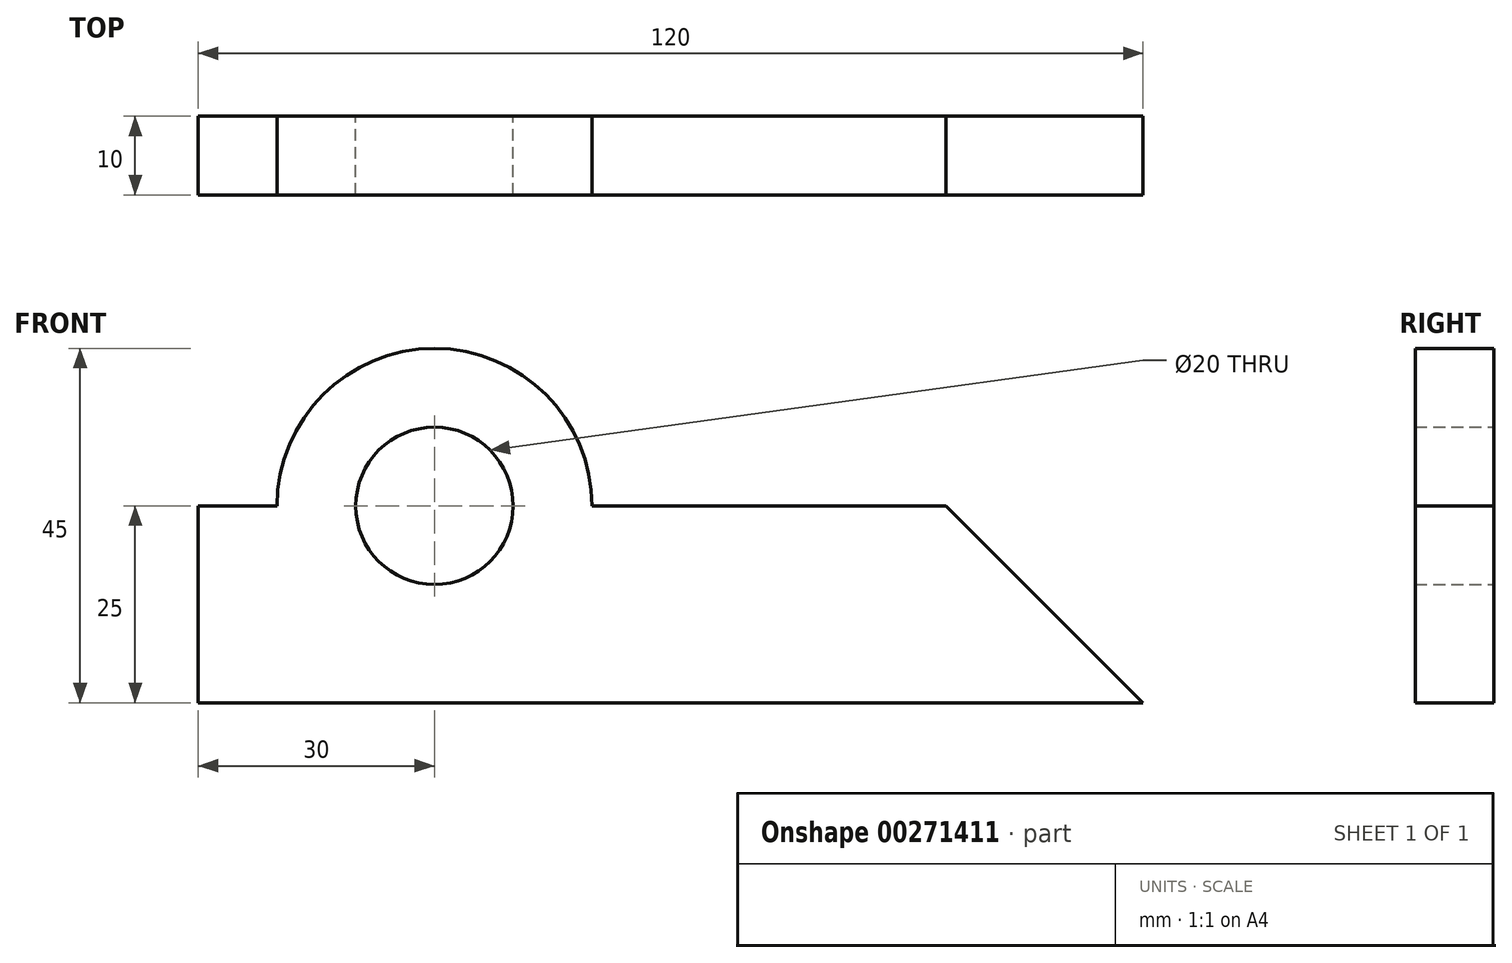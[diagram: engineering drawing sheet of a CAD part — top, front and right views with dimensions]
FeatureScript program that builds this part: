
annotation { "Feature Type Name" : "Feature", "Feature Type Description" : "" }
export const myFeature = defineFeature(function(context is Context, id is Id, definition is map)
    precondition{}
    {
        {
            var Q0;
            Q0=qCreatedBy(makeId("Front.planeOp"),FACE);
            var sketch = newSketch(context, id + "F0", { "sketchPlane" : qUnion([Q0])});
            skLineSegment(sketch, "E0", {"start": v(0, 0) * mm, "end": v(0, 25) * mm});
            skLineSegment(sketch, "E1", {"start": v(0, 0) * mm, "end": v(120, 0) * mm});
            skLineSegment(sketch, "E2", {"start": v(120, 0) * mm, "end": v(95, 25) * mm});
            skLineSegment(sketch, "E3", {"start": v(95, 25) * mm, "end": v(50, 25) * mm});
            skLineSegment(sketch, "E4", {"start": v(0, 25) * mm, "end": v(10, 25) * mm});
            skPoint(sketch, "E5", {"position": v(30, 25) * mm});
            skCircle(sketch, "E6", {"center": v(30, 25) * mm, "radius": 10 * mm});
            skArc(sketch, "E7", {"start": v(50, 25) * mm, "mid": v(30, 45) * mm, "end": v(10, 25) * mm});
            skSolve(sketch);
        }
        {
            var Q0;
            Q0=makeQuery(id+"F0.imprint","IMPRINT",FACE,{"disambiguationData":[TD([[makeQuery(id+"F0.imprint","IMPRINT",EDGE,{"derivedFrom":sQuery(id+"F0.wireOp",EDGE,"E0")}),-1.0]])]});
            extrude(context, id + "F1", {"entities" : qUnion([Q0]), "depth" : 10 * mm});
        }
    });
